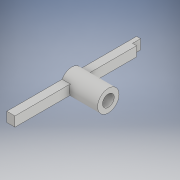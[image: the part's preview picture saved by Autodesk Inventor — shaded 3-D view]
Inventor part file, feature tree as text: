
AUTODESK INVENTOR PART (.ipt)
format: ipt  version: 2019 (Build 230136000, 136)  size: 162,304 bytes
history: native  units: in
note: dims shown in document units (in); Inventor stores cm internally (conversion verified against a paired STEP export)
features: extrude x6, sketch x6, projected_geometry x3
ambient origin geometry x8: Origin, YZ Plane, XZ Plane, XY Plane, X Axis, Y Axis, Z Axis, Center Point
bodies: Solid1 (feature_tree)
feature tree (15):
  extrude  "Extrusion1"  Depth=0.36in
  extrude  "Extrusion2"  Depth=0.1in TaperAngle=0.0deg
  extrude  "Extrusion7"  TaperAngle=0.0deg  [1 undecoded]
  extrude  "Extrusion18"  TaperAngle=0.0deg  [1 undecoded]
  extrude  "Extrusion19"  Depth=4.0in
  extrude  "Extrusion20"  Depth=0.25in
  sketch  "Sketch1"  dims[d0=0.36in d1=0.15in]
  sketch  "Sketch2"  dims[d2=0.78in d3=0.0in d4=0.1in d5=0.0in]
  sketch  "Sketch10"  dims[d28=0.875in d29=0.0in d42=0.0in]
  sketch  "Sketch24"  dims[d43=0.0in d44=0.0in]
  projected_geometry  "Projected Loop15"
  sketch  "Sketch25"  dims[d90=4.0in d91=2.0in]
  projected_geometry  "Projected Loop16"
  projected_geometry  "Projected Loop17"
  sketch  "Sketch26"  dims[d92=0.15in d93=0.15in d94=0.25in d95=0.0in d96=0.25in d97=0.0in d98=0.125in d99=0.25in d100=1.0in d101=0.0in]
note: 2 required parameter values undecoded (feature->parameter linkage not recoverable at this tier; creation-order binding heuristic only, values carry confidence <= 0.55)
